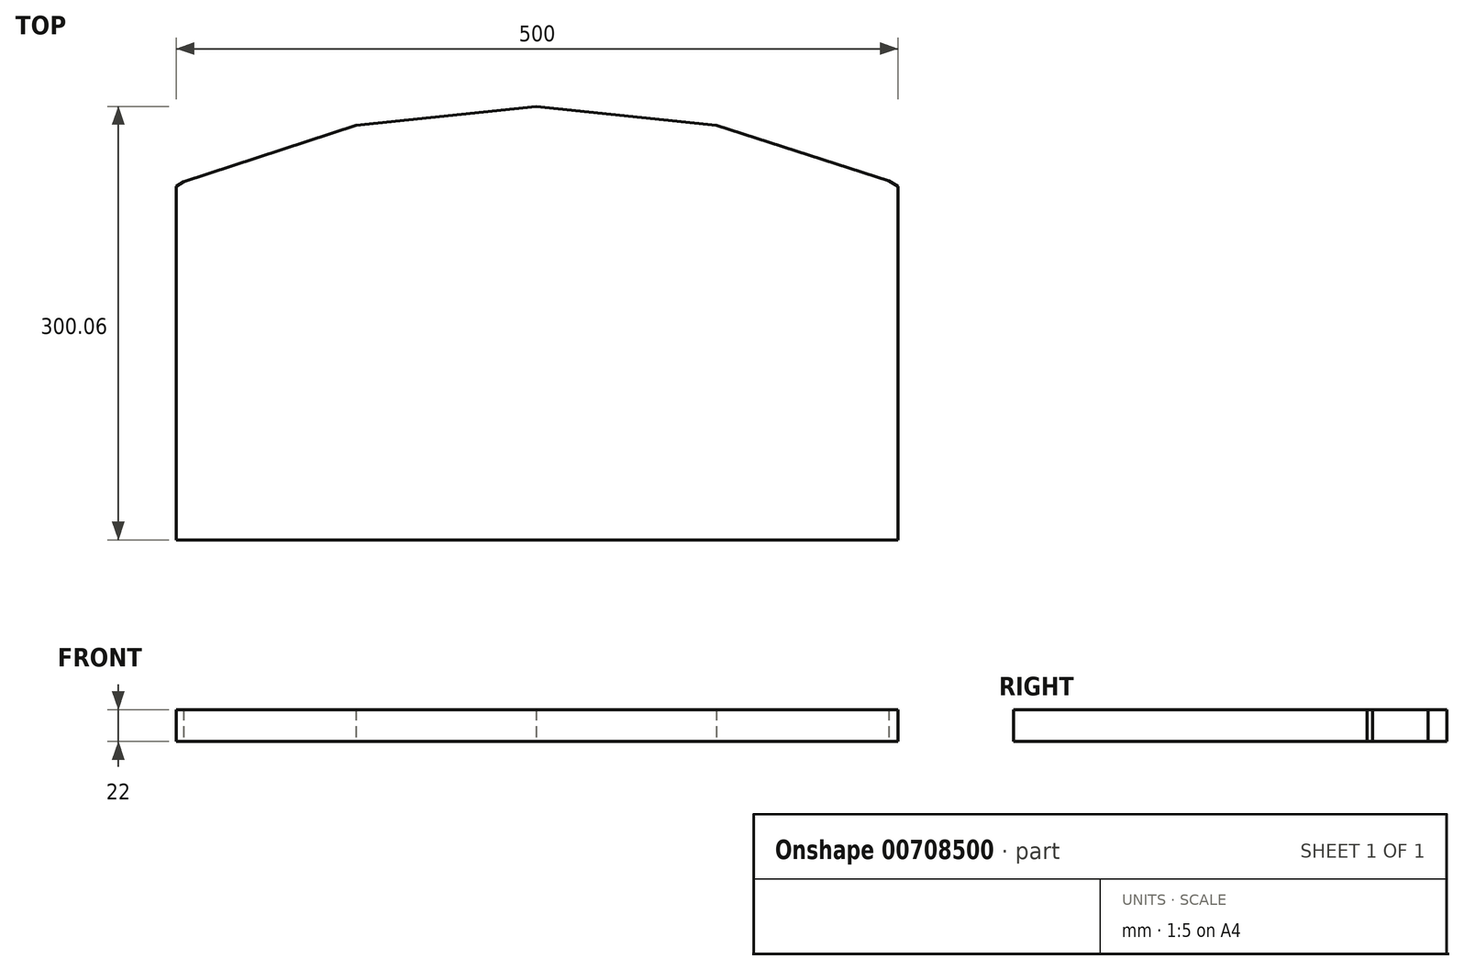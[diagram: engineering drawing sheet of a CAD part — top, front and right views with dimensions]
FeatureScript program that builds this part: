
annotation { "Feature Type Name" : "Feature", "Feature Type Description" : "" }
export const myFeature = defineFeature(function(context is Context, id is Id, definition is map)
    precondition{}
    {
        {
            var Q0;
            Q0=qCreatedBy(makeId("Top.planeOp"),FACE);
            var sketch = newSketch(context, id + "F0", { "sketchPlane" : qUnion([Q0])});
            skLineSegment(sketch, "E0.top", {"start": v(-250, 300) * mm, "end": v(250, 300) * mm});
            skPoint(sketch, "E0.middle", {"position": v(0, 0) * mm});
            skPoint(sketch, "E1.end.orphan", {"position": v(-300, -300) * mm});
            skLineSegment(sketch, "E2.17", {"start": v(-250, 544.85) * mm, "end": v(-244.7, 547.91) * mm});
            skLineSegment(sketch, "E2.18", {"start": v(-244.7, 547.91) * mm, "end": v(-125.4, 586.82) * mm});
            skLineSegment(sketch, "E2.19", {"start": v(-125.4, 586.82) * mm, "end": v(-0.6, 600.06) * mm});
            skLineSegment(sketch, "E2.20", {"start": v(-0.6, 600.06) * mm, "end": v(124.23, 587.06) * mm});
            skLineSegment(sketch, "E2.21", {"start": v(124.23, 587.06) * mm, "end": v(243.62, 548.37) * mm});
            skLineSegment(sketch, "E2.22", {"start": v(243.62, 548.37) * mm, "end": v(250, 544.7) * mm});
            skPoint(sketch, "E3.visualSharp", {"position": v(-300, 300) * mm});
            skPoint(sketch, "E4.visualSharp", {"position": v(-300, -52.1) * mm});
            skPoint(sketch, "E5.visualSharp", {"position": v(300, 300) * mm});
            skLineSegment(sketch, "E6", {"start": v(-300, -2.1) * mm, "end": v(-300, -2.1) * mm});
            skLineSegment(sketch, "E7", {"start": v(250, 300) * mm, "end": v(250, 544.7) * mm});
            skLineSegment(sketch, "E8", {"start": v(-250, 300) * mm, "end": v(-250, 544.85) * mm});
            skPoint(sketch, "E0.right.start.orphan", {"position": v(300, -300) * mm});
            skSolve(sketch);
        }
        {
            var Q0;
            Q0=qSketchRegion(id+"F0",true);
            extrude(context, id + "F1", {"entities" : qUnion([Q0]), "depth" : 22 * mm, "offsetDistance" : 25 * mm});
        }
    });
